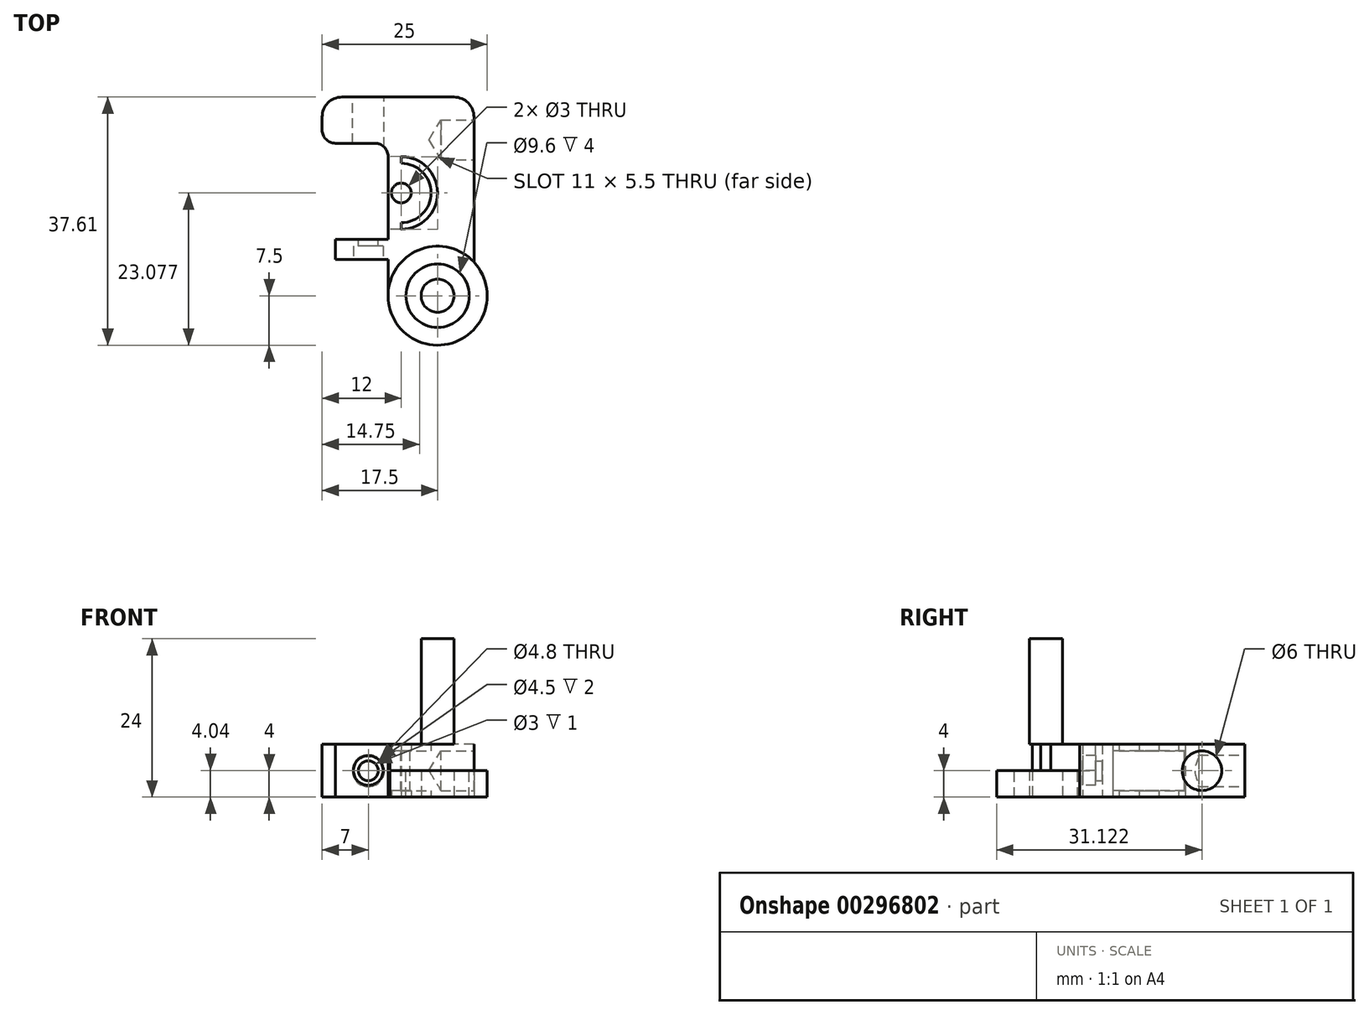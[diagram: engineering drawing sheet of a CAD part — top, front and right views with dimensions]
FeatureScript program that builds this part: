
annotation { "Feature Type Name" : "Feature", "Feature Type Description" : "" }
export const myFeature = defineFeature(function(context is Context, id is Id, definition is map)
    precondition{}
    {
        {
            var Q0;
            Q0=qCreatedBy(makeId("Top.planeOp"),FACE);
            var sketch = newSketch(context, id + "F0", { "sketchPlane" : qUnion([Q0])});
            skLineSegment(sketch, "E0.bottom", {"start": v(-21.15, 21.15) * mm, "end": v(21.15, 21.15) * mm});
            skLineSegment(sketch, "E0.top", {"start": v(-21.15, -21.15) * mm, "end": v(21.15, -21.15) * mm});
            skLineSegment(sketch, "E0.left", {"start": v(-21.15, 21.15) * mm, "end": v(-21.15, -21.15) * mm});
            skLineSegment(sketch, "E0.right", {"start": v(21.15, 21.15) * mm, "end": v(21.15, -21.15) * mm});
            skPoint(sketch, "E1", {"position": v(-15.5, 15.5) * mm});
            skPoint(sketch, "E2.0.1.0", {"position": v(-15.5, -15.5) * mm});
            skPoint(sketch, "E2.1.0.0", {"position": v(15.5, 15.5) * mm});
            skPoint(sketch, "E2.1.1.0", {"position": v(15.5, -15.5) * mm});
            skLineSegment(sketch, "E2.direction1", {"start": v(-15.5, 15.5) * mm, "end": v(15.5, 15.5) * mm, "construction": true});
            skLineSegment(sketch, "E2.direction2", {"start": v(-15.5, 15.5) * mm, "end": v(-15.5, -15.5) * mm, "construction": true});
            skCircle(sketch, "E3", {"center": v(-15.5, 15.5) * mm, "radius": 1.5 * mm});
            skCircle(sketch, "E4", {"center": v(15.5, 15.5) * mm, "radius": 1.5 * mm});
            skCircle(sketch, "E5", {"center": v(15.5, -15.5) * mm, "radius": 1.5 * mm});
            skCircle(sketch, "E6", {"center": v(-15.5, -15.5) * mm, "radius": 1.5 * mm});
            skCircle(sketch, "E7", {"center": v(0, 0) * mm, "radius": 2.5 * mm});
            skCircle(sketch, "E8", {"center": v(0, 0) * mm, "radius": 3.5 * mm, "construction": true});
            skCircle(sketch, "E9", {"center": v(0, 0) * mm, "radius": 11 * mm});
            skSolve(sketch);
        }
        {
            var Q0;
            Q0=makeQuery(id+"F0.imprint","IMPRINT",FACE,{"disambiguationData":[TD([[makeQuery(id+"F0.imprint","IMPRINT",EDGE,{"derivedFrom":sQuery(id+"F0.wireOp",EDGE,"E7")}),1.0]])]});
            extrude(context, id + "F1", {"entities" : qUnion([Q0]), "depth" : 24 * mm});
        }
        {
            var Q0;
            Q0=makeQuery(id+"F0.imprint","IMPRINT",FACE,{"disambiguationData":[TD([[makeQuery(id+"F0.imprint","IMPRINT",EDGE,{"derivedFrom":sQuery(id+"F0.wireOp",EDGE,"E0.top")}),1.0]])]});
            var sketch = newSketch(context, id + "F2", { "sketchPlane" : qUnion([Q0])});
            skCircle(sketch, "E10", {"center": v(0, 0) * mm, "radius": 2.6 * mm});
            skCircle(sketch, "E11", {"center": v(0, 0) * mm, "radius": 5.5 * mm});
            skCircle(sketch, "E12", {"center": v(-15.5, 15.58) * mm, "radius": 4.5 * mm, "construction": true});
            skPoint(sketch, "E13.visualSharp", {"position": v(5, 19.88) * mm});
            skPoint(sketch, "E14.visualSharp", {"position": v(-7.7, 18.94) * mm});
            skLineSegment(sketch, "E15", {"start": v(-7.54, 17.74) * mm, "end": v(-7.55, 17.84) * mm});
            skPoint(sketch, "E16.visualSharp", {"position": v(-7.7, 19.9) * mm});
            skLineSegment(sketch, "E17", {"start": v(5.5, 0) * mm, "end": v(5.5, 30.1) * mm});
            skLineSegment(sketch, "E18", {"start": v(5.5, 30.1) * mm, "end": v(-5.5, 30.1) * mm});
            skCircle(sketch, "E19", {"center": v(-5.5, 15.58) * mm, "radius": 4.5 * mm, "construction": true});
            skArc(sketch, "E20", {"start": v(-5.5, 10.08) * mm, "mid": v(0, 15.58) * mm, "end": v(-5.5, 21.08) * mm});
            skPoint(sketch, "E21.visualSharp", {"position": v(-5.5, 10.08) * mm});
            skArc(sketch, "E22", {"start": v(-5.5, 11.08) * mm, "mid": v(-1, 15.58) * mm, "end": v(-5.5, 20.08) * mm});
            skLineSegment(sketch, "E23", {"start": v(-5.5, 11.08) * mm, "end": v(-5.5, 10.08) * mm});
            skLineSegment(sketch, "E24", {"start": v(-5.5, 20.08) * mm, "end": v(-5.5, 21.08) * mm});
            skLineSegment(sketch, "E25", {"start": v(-9.5, 23.1) * mm, "end": v(-15.5, 23.1) * mm});
            skLineSegment(sketch, "E26", {"start": v(-17.5, 25.1) * mm, "end": v(-17.5, 30.1) * mm});
            skLineSegment(sketch, "E27", {"start": v(-17.5, 30.1) * mm, "end": v(-5.5, 30.1) * mm});
            skLineSegment(sketch, "E28", {"start": v(-7.5, 21.1) * mm, "end": v(-7.5, 10.1) * mm});
            skLineSegment(sketch, "E29", {"start": v(-7.5, 10.1) * mm, "end": v(-7.47, 8.51) * mm});
            skPoint(sketch, "E30.visualSharp", {"position": v(-7.42, 6.55) * mm});
            skCircle(sketch, "E31", {"center": v(-5.5, 15.58) * mm, "radius": 1.5 * mm});
            skPoint(sketch, "E32.visualSharp", {"position": v(-7.5, 23.1) * mm});
            skArc(sketch, "E32.filletArc", {"start": v(-7.5, 21.1) * mm, "mid": v(-8.09, 22.52) * mm, "end": v(-9.5, 23.1) * mm});
            skPoint(sketch, "E33.visualSharp", {"position": v(-17.5, 23.1) * mm});
            skArc(sketch, "E33.filletArc", {"start": v(-17.5, 25.1) * mm, "mid": v(-16.91, 23.7) * mm, "end": v(-15.5, 23.1) * mm});
            skLineSegment(sketch, "E34", {"start": v(-7.47, 8.51) * mm, "end": v(-7.47, -0.49) * mm});
            skLineSegment(sketch, "E35", {"start": v(-2.49, -5.49) * mm, "end": v(0, -5.5) * mm});
            skPoint(sketch, "E36.visualSharp", {"position": v(-7.47, -5.47) * mm});
            skArc(sketch, "E36.filletArc", {"start": v(-7.47, -0.49) * mm, "mid": v(-6, -4.02) * mm, "end": v(-2.49, -5.49) * mm});
            skLineSegment(sketch, "E37.bottom", {"start": v(-7.47, 8.51) * mm, "end": v(-15.47, 8.51) * mm});
            skLineSegment(sketch, "E37.top", {"start": v(-7.47, 5.51) * mm, "end": v(-15.47, 5.51) * mm});
            skLineSegment(sketch, "E37.left", {"start": v(-7.47, 8.51) * mm, "end": v(-7.47, 5.51) * mm});
            skLineSegment(sketch, "E37.right", {"start": v(-15.47, 8.51) * mm, "end": v(-15.47, 5.51) * mm});
            skSolve(sketch);
        }
        {
            var Q0;
            Q0=qSketchRegion(id+"F2",true);
            extrude(context, id + "F3", {"entities" : qUnion([Q0]), "depth" : 8 * mm});
        }
        {
            var Q0;
            Q0=qCreatedBy(makeId("Top.planeOp"),FACE);
            cPlane(context, id + "F4", {"entities" : qUnion([Q0]), "cplaneType" : CPlaneType.OFFSET, "offset" : 4 * mm, "width" : 150 * mm, "height" : 150 * mm});
        }
        {
            var Q0;
            Q0=qCreatedBy(id+"F4.planeOp",FACE);
            var sketch = newSketch(context, id + "F5", { "sketchPlane" : qUnion([Q0])});
            skArc(sketch, "E38", {"start": v(-5.65, 10.1) * mm, "mid": v(-0.07, 15.59) * mm, "end": v(-5.64, 21.1) * mm});
            skLineSegment(sketch, "E39", {"start": v(-5.5, 10.1) * mm, "end": v(-11.5, 10.1) * mm});
            skLineSegment(sketch, "E40", {"start": v(-5.64, 21.1) * mm, "end": v(-11.64, 21.02) * mm});
            skLineSegment(sketch, "E41", {"start": v(-11.64, 21.02) * mm, "end": v(-11.5, 10.1) * mm});
            skSolve(sketch);
        }
        {
            var Q0;
            Q0=qSketchRegion(id+"F5",true);
            extrude(context, id + "F6", {"entities" : qUnion([Q0]), "operationType" : NewBodyOperationType.REMOVE, "depth" : 3 * mm, "hasSecondDirection" : true, "secondDirectionOppositeDirection" : true, "secondDirectionDepth" : 3 * mm});
        }
        {
            var Q0;
            Q0=makeQuery(id+"F3.opExtrude","CAP_FACE",FACE,{"disambiguationData":[OSD([sQuery(id+"F2.wireOp",EDGE,"E10"),sQuery(id+"F2.wireOp",EDGE,"E11"),sQuery(id+"F2.wireOp",EDGE,"WF9XXERk-SnKw-Fhc3-FHvs-27cXdYq0G9Vx"),sQuery(id+"F2.wireOp",EDGE,"E17"),sQuery(id+"F2.wireOp",EDGE,"E18"),sQuery(id+"F2.wireOp",EDGE,"E20"),sQuery(id+"F2.wireOp",EDGE,"E22"),sQuery(id+"F2.wireOp",EDGE,"E23"),sQuery(id+"F2.wireOp",EDGE,"E24"),sQuery(id+"F2.wireOp",EDGE,"E25"),sQuery(id+"F2.wireOp",EDGE,"E26"),sQuery(id+"F2.wireOp",EDGE,"E27"),sQuery(id+"F2.wireOp",EDGE,"E28"),sQuery(id+"F2.wireOp",EDGE,"E29"),sQuery(id+"F2.wireOp",EDGE,"E30.filletArc"),sQuery(id+"F2.wireOp",EDGE,"E31")])],"isStart":false});
            var sketch = newSketch(context, id + "F7", { "sketchPlane" : qUnion([Q0])});
            skCircle(sketch, "E42", {"center": v(0, 0) * mm, "radius": 7.5 * mm});
            skSolve(sketch);
        }
        {
            var Q0;
            Q0=qSketchRegion(id+"F7",true);
            extrude(context, id + "F8", {"entities" : qUnion([Q0]), "operationType" : NewBodyOperationType.REMOVE, "oppositeDirection" : true, "depth" : 4 * mm});
        }
        {
            var Q0;
            Q0=makeQuery(id+"F3.opExtrude","SWEPT_FACE",FACE,{"disambiguationData":[OSD([sQuery(id+"F2.wireOp",EDGE,"E18"),sQuery(id+"F2.wireOp",EDGE,"E27")])]});
            var sketch = newSketch(context, id + "F9", { "sketchPlane" : qUnion([Q0])});
            skPoint(sketch, "E43", {"position": v(10.5, 4) * mm});
            skSolve(sketch);
        }
        {
            var Q0;
            Q0=sQuery(id+"F9.wireOp",VERTEX,"E43");
            var Q1;
            Q1=makeQuery(id+"F3.opExtrude","SWEPT_BODY",BODY,{"disambiguationData":[OSD([sQuery(id+"F2.wireOp",EDGE,"E10"),sQuery(id+"F2.wireOp",EDGE,"E11"),sQuery(id+"F2.wireOp",EDGE,"WF9XXERk-SnKw-Fhc3-FHvs-27cXdYq0G9Vx"),sQuery(id+"F2.wireOp",EDGE,"E17"),sQuery(id+"F2.wireOp",EDGE,"E18"),sQuery(id+"F2.wireOp",EDGE,"E20"),sQuery(id+"F2.wireOp",EDGE,"E22"),sQuery(id+"F2.wireOp",EDGE,"E23"),sQuery(id+"F2.wireOp",EDGE,"E24"),sQuery(id+"F2.wireOp",EDGE,"E25"),sQuery(id+"F2.wireOp",EDGE,"E26"),sQuery(id+"F2.wireOp",EDGE,"E27"),sQuery(id+"F2.wireOp",EDGE,"E28"),sQuery(id+"F2.wireOp",EDGE,"E29"),sQuery(id+"F2.wireOp",EDGE,"E30.filletArc"),sQuery(id+"F2.wireOp",EDGE,"E31"),sQuery(id+"F2.wireOp",EDGE,"E32.filletArc"),sQuery(id+"F2.wireOp",EDGE,"E33.filletArc")])]});
            hole(context, id + "F10", {"style" : HoleStyle.SIMPLE, "endStyle" : HoleEndStyle.BLIND, "holeDiameter" : 4.8 * mm, "holeDepth" : 10 * mm, "locations" : qUnion([Q0]), "scope" : qUnion([Q1]), "tappedDepth" : 12 * mm, "tapClearance" : 3});
        }
        {
            var Q0;
            Q0=makeQuery(id+"F3.opExtrude","SWEPT_FACE",FACE,{"disambiguationData":[OSD([sQuery(id+"F2.wireOp",EDGE,"E17")])]});
            var sketch = newSketch(context, id + "F11", { "sketchPlane" : qUnion([Q0])});
            skCircle(sketch, "E44", {"center": v(23.62, 4) * mm, "radius": 3 * mm});
            skSolve(sketch);
        }
        {
            var Q0;
            Q0=sQuery(id+"F11.wireOp",VERTEX,"E44.center");
            var Q1;
            Q1=makeQuery(id+"F3.opExtrude","SWEPT_BODY",BODY,{"disambiguationData":[OSD([sQuery(id+"F2.wireOp",EDGE,"E10"),sQuery(id+"F2.wireOp",EDGE,"E11"),sQuery(id+"F2.wireOp",EDGE,"WF9XXERk-SnKw-Fhc3-FHvs-27cXdYq0G9Vx"),sQuery(id+"F2.wireOp",EDGE,"E17"),sQuery(id+"F2.wireOp",EDGE,"E18"),sQuery(id+"F2.wireOp",EDGE,"E20"),sQuery(id+"F2.wireOp",EDGE,"E22"),sQuery(id+"F2.wireOp",EDGE,"E23"),sQuery(id+"F2.wireOp",EDGE,"E24"),sQuery(id+"F2.wireOp",EDGE,"E25"),sQuery(id+"F2.wireOp",EDGE,"E26"),sQuery(id+"F2.wireOp",EDGE,"E27"),sQuery(id+"F2.wireOp",EDGE,"E28"),sQuery(id+"F2.wireOp",EDGE,"E29"),sQuery(id+"F2.wireOp",EDGE,"E30.filletArc"),sQuery(id+"F2.wireOp",EDGE,"E31"),sQuery(id+"F2.wireOp",EDGE,"E32.filletArc"),sQuery(id+"F2.wireOp",EDGE,"E33.filletArc")])]});
            hole(context, id + "F12", {"style" : HoleStyle.SIMPLE, "endStyle" : HoleEndStyle.BLIND, "holeDiameter" : 6 * mm, "holeDepth" : 5 * mm, "locations" : qUnion([Q0]), "scope" : qUnion([Q1])});
        }
        {
            var Q0;
            Q0=makeQuery(id+"F3.opExtrude","SWEPT_EDGE",EDGE,{"disambiguationData":[OSD([sQuery(id+"F2.wireOp",EDGE,"E17"),sQuery(id+"F2.wireOp",EDGE,"E18")])]});
            fillet(context, id + "F13", {"entities" : qUnion([Q0]), "radius" : 3 * mm, "tangentPropagation" : true, "allowEdgeOverflow" : false});
        }
        {
            var Q0;
            Q0=makeQuery(id+"F3.opExtrude","SWEPT_EDGE",EDGE,{"disambiguationData":[OSD([sQuery(id+"F2.wireOp",EDGE,"E26"),sQuery(id+"F2.wireOp",EDGE,"E27")])]});
            fillet(context, id + "F14", {"entities" : qUnion([Q0]), "radius" : 3 * mm, "tangentPropagation" : true, "allowEdgeOverflow" : false});
        }
        {
            var Q0;
            Q0=makeQuery(id+"F3.opExtrude","CAP_FACE",FACE,{"disambiguationData":[OSD([sQuery(id+"F2.wireOp",EDGE,"E10"),sQuery(id+"F2.wireOp",EDGE,"E11"),sQuery(id+"F2.wireOp",EDGE,"WF9XXERk-SnKw-Fhc3-FHvs-27cXdYq0G9Vx"),sQuery(id+"F2.wireOp",EDGE,"E17"),sQuery(id+"F2.wireOp",EDGE,"E18"),sQuery(id+"F2.wireOp",EDGE,"E20"),sQuery(id+"F2.wireOp",EDGE,"E22"),sQuery(id+"F2.wireOp",EDGE,"E23"),sQuery(id+"F2.wireOp",EDGE,"E24"),sQuery(id+"F2.wireOp",EDGE,"E25"),sQuery(id+"F2.wireOp",EDGE,"E26"),sQuery(id+"F2.wireOp",EDGE,"E27"),sQuery(id+"F2.wireOp",EDGE,"E28"),sQuery(id+"F2.wireOp",EDGE,"E29"),sQuery(id+"F2.wireOp",EDGE,"E30.filletArc"),sQuery(id+"F2.wireOp",EDGE,"E31"),sQuery(id+"F2.wireOp",EDGE,"E32.filletArc"),sQuery(id+"F2.wireOp",EDGE,"E33.filletArc")])],"isStart":true});
            var sketch = newSketch(context, id + "F15", { "sketchPlane" : qUnion([Q0])});
            skCircle(sketch, "E45", {"center": v(0, 0) * mm, "radius": 7.5 * mm});
            skSolve(sketch);
        }
        {
            var Q0;
            {var subQ5=makeQuery(id+"F3.opExtrude","CAP_EDGE",EDGE,{"disambiguationData":[OSD([sQuery(id+"F2.wireOp",EDGE,"E11")])],"isStart":true});Q0=makeQuery(id+"F15.imprint","IMPRINT",FACE,{"disambiguationData":[TD([[makeQuery(id+"F15.imprint","IMPRINT",EDGE,{"derivedFrom":subQ5}),1.0]])]});}
            var Q1;
            Q1=makeQuery(id+"F15.imprint","IMPRINT",FACE,{"disambiguationData":[TD([[makeQuery(id+"F15.imprint","IMPRINT",EDGE,{"derivedFrom":makeQuery(id+"F3.opExtrude","CAP_EDGE",EDGE,{"disambiguationData":[OSD([sQuery(id+"F2.wireOp",EDGE,"E10")])],"isStart":true})}),1.0]])]});
            extrude(context, id + "F16", {"entities" : qUnion([Q0, Q1]), "operationType" : NewBodyOperationType.ADD, "oppositeDirection" : true, "depth" : 4 * mm});
        }
        {
            var Q0;
            Q0=makeQuery(id+"F16.opExtrude","CAP_FACE",FACE,{"disambiguationData":[OSD([sQuery(id+"F2.wireOp",EDGE,"E10"),sQuery(id+"F15.wireOp",EDGE,"E45")])],"isStart":false});
            var sketch = newSketch(context, id + "F17", { "sketchPlane" : qUnion([Q0])});
            skCircle(sketch, "E46", {"center": v(0, 0) * mm, "radius": 4.8 * mm});
            skSolve(sketch);
        }
        {
            var Q0;
            Q0=makeQuery(id+"F17.imprint","IMPRINT",FACE,{"disambiguationData":[TD([[makeQuery(id+"F17.imprint","IMPRINT",EDGE,{"derivedFrom":sQuery(id+"F17.wireOp",EDGE,"E46")}),1.0]])]});
            extrude(context, id + "F18", {"entities" : qUnion([Q0]), "operationType" : NewBodyOperationType.REMOVE, "oppositeDirection" : true, "depth" : 4 * mm});
        }
        {
            var Q0;
            Q0=makeQuery(id+"F3.opExtrude","SWEPT_FACE",FACE,{"disambiguationData":[OSD([sQuery(id+"F2.wireOp",EDGE,"E37.top")])]});
            var sketch = newSketch(context, id + "F19", { "sketchPlane" : qUnion([Q0])});
            skCircle(sketch, "E47", {"center": v(-10.5, 4.04) * mm, "radius": 2.25 * mm});
            skSolve(sketch);
        }
        {
            var Q0;
            Q0=makeQuery(id+"F19.imprint","IMPRINT",FACE,{"disambiguationData":[TD([[makeQuery(id+"F19.imprint","IMPRINT",EDGE,{"derivedFrom":sQuery(id+"F19.wireOp",EDGE,"E47")}),1.0]])]});
            extrude(context, id + "F20", {"entities" : qUnion([Q0]), "operationType" : NewBodyOperationType.REMOVE, "oppositeDirection" : true, "depth" : 2 * mm});
        }
        {
            var Q0;
            Q0=sQuery(id+"F9.wireOp",VERTEX,"E43");
            var Q1;
            Q1=makeQuery(id+"F3.opExtrude","SWEPT_BODY",BODY,{"disambiguationData":[OSD([sQuery(id+"F2.wireOp",EDGE,"E10"),sQuery(id+"F2.wireOp",EDGE,"E11"),sQuery(id+"F2.wireOp",EDGE,"E17"),sQuery(id+"F2.wireOp",EDGE,"E18"),sQuery(id+"F2.wireOp",EDGE,"E20"),sQuery(id+"F2.wireOp",EDGE,"E22"),sQuery(id+"F2.wireOp",EDGE,"E23"),sQuery(id+"F2.wireOp",EDGE,"E24"),sQuery(id+"F2.wireOp",EDGE,"E25"),sQuery(id+"F2.wireOp",EDGE,"E26"),sQuery(id+"F2.wireOp",EDGE,"E27"),sQuery(id+"F2.wireOp",EDGE,"E28"),sQuery(id+"F2.wireOp",EDGE,"E29"),sQuery(id+"F2.wireOp",EDGE,"E31"),sQuery(id+"F2.wireOp",EDGE,"E32.filletArc"),sQuery(id+"F2.wireOp",EDGE,"E33.filletArc"),sQuery(id+"F2.wireOp",EDGE,"E34"),sQuery(id+"F2.wireOp",EDGE,"E35"),sQuery(id+"F2.wireOp",EDGE,"E36.filletArc"),sQuery(id+"F2.wireOp",EDGE,"E37.bottom"),sQuery(id+"F2.wireOp",EDGE,"E37.top"),sQuery(id+"F2.wireOp",EDGE,"E37.right")])]});
            hole(context, id + "F21", {"style" : HoleStyle.SIMPLE, "endStyle" : HoleEndStyle.BLIND, "holeDiameter" : 3 * mm, "holeDepth" : 5 * mm, "tappedDepth" : 12 * mm, "tapClearance" : 3, "locations" : qUnion([Q0]), "scope" : qUnion([Q1])});
        }
    });
